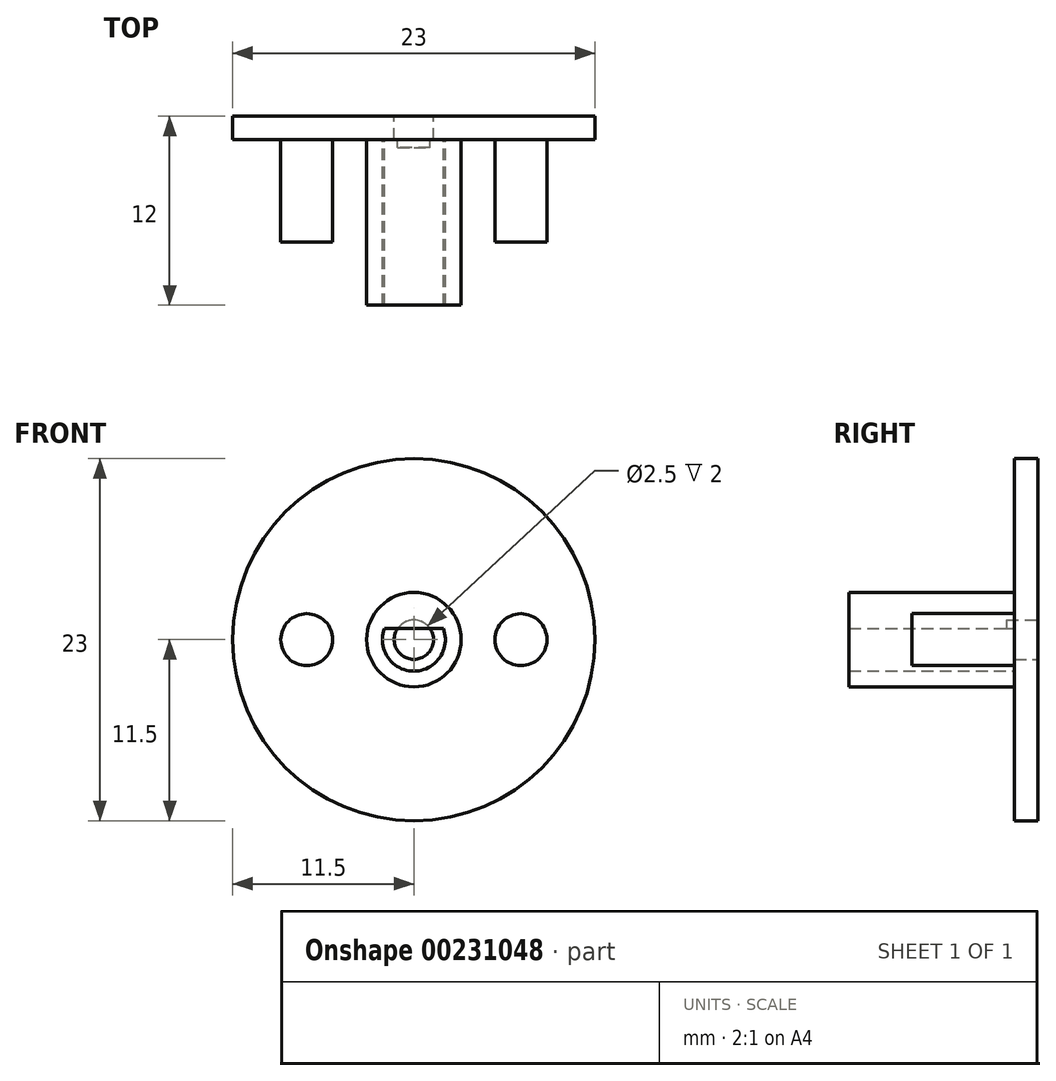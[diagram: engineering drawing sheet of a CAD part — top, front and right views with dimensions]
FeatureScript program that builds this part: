
annotation { "Feature Type Name" : "Feature", "Feature Type Description" : "" }
export const myFeature = defineFeature(function(context is Context, id is Id, definition is map)
    precondition{}
    {
        {
            var Q0;
            Q0=qCreatedBy(makeId("Front.planeOp"),FACE);
            var sketch = newSketch(context, id + "F0", { "sketchPlane" : qUnion([Q0])});
            skCircle(sketch, "E0", {"center": v(0, 0) * mm, "radius": 3 * mm});
            skCircle(sketch, "E1", {"center": v(6.5, 0) * mm, "radius": 1.8 * mm});
            skCircle(sketch, "E2", {"center": v(0, 0) * mm, "radius": 11.5 * mm});
            skSolve(sketch);
        }
        {
            var Q0;
            Q0=makeQuery(id+"F0.imprint","IMPRINT",FACE,{"disambiguationData":[TD([[makeQuery(id+"F0.imprint","IMPRINT",EDGE,{"derivedFrom":sQuery(id+"F0.wireOp",EDGE,"E0")}),-1.0]])]});
            var Q1;
            Q1=makeQuery(id+"F0.imprint","IMPRINT",FACE,{"disambiguationData":[TD([[makeQuery(id+"F0.imprint","IMPRINT",EDGE,{"derivedFrom":sQuery(id+"F0.wireOp",EDGE,"E0")}),1.0]])]});
            var Q2;
            Q2=makeQuery(id+"F0.imprint","IMPRINT",FACE,{"disambiguationData":[TD([[makeQuery(id+"F0.imprint","IMPRINT",EDGE,{"derivedFrom":sQuery(id+"F0.wireOp",EDGE,"E1")}),1.0]])]});
            extrude(context, id + "F1", {"entities" : qUnion([Q0, Q1, Q2]), "depth" : 1.5 * mm});
        }
        {
            var Q0;
            Q0=makeQuery(id+"F1.opExtrude","CAP_FACE",FACE,{"disambiguationData":[OSD([sQuery(id+"F0.wireOp",EDGE,"E2")])],"isStart":false});
            var sketch = newSketch(context, id + "F2", { "sketchPlane" : qUnion([Q0])});
            skCircle(sketch, "E3", {"center": v(0, 0) * mm, "radius": 3 * mm});
            skCircle(sketch, "E4", {"center": v(6.8, 0) * mm, "radius": 1.65 * mm});
            skCircle(sketch, "E5", {"center": v(-6.8, 0) * mm, "radius": 1.65 * mm});
            skCircle(sketch, "E6", {"center": v(0, 0) * mm, "radius": 2 * mm});
            skLineSegment(sketch, "E7", {"start": v(-1.87, 0.7) * mm, "end": v(1.87, 0.7) * mm});
            skSolve(sketch);
        }
        {
            var Q0;
            Q0=makeQuery(id+"F2.imprint","IMPRINT",FACE,{"disambiguationData":[TD([[makeQuery(id+"F2.imprint","IMPRINT",EDGE,{"derivedFrom":sQuery(id+"F2.wireOp",EDGE,"E5")}),1.0]])]});
            var Q1;
            Q1=makeQuery(id+"F2.imprint","IMPRINT",FACE,{"disambiguationData":[TD([[makeQuery(id+"F2.imprint","IMPRINT",EDGE,{"derivedFrom":sQuery(id+"F2.wireOp",EDGE,"E3")}),1.0]])]});
            var Q2;
            {var subQ0=sQuery(id+"F2.wireOp",EDGE,"E7");Q2=makeQuery(id+"F2.imprint","IMPRINT",FACE,{"disambiguationData":[TD([[makeQuery(id+"F2.imprint","IMPRINT",EDGE,{"derivedFrom":subQ0}),1.0]])]});}
            var Q3;
            Q3=makeQuery(id+"F2.imprint","IMPRINT",FACE,{"disambiguationData":[TD([[makeQuery(id+"F2.imprint","IMPRINT",EDGE,{"derivedFrom":sQuery(id+"F2.wireOp",EDGE,"E4")}),1.0]])]});
            extrude(context, id + "F3", {"entities" : qUnion([Q0, Q1, Q2, Q3]), "operationType" : NewBodyOperationType.ADD, "depth" : 6.5 * mm});
        }
        {
            var Q0;
            Q0=makeQuery(id+"F3.opExtrude","CAP_FACE",FACE,{"disambiguationData":[OSD([sQuery(id+"F2.wireOp",EDGE,"E3"),sQuery(id+"F2.wireOp",EDGE,"E6"),sQuery(id+"F2.wireOp",EDGE,"E7")])],"isStart":false});
            extrude(context, id + "F4", {"entities" : qUnion([Q0]), "operationType" : NewBodyOperationType.ADD, "depth" : 4 * mm});
        }
        {
            var Q0;
            Q0=makeQuery(id+"F1.opExtrude","CAP_FACE",FACE,{"disambiguationData":[OSD([sQuery(id+"F0.wireOp",EDGE,"E2")])],"isStart":true});
            var sketch = newSketch(context, id + "F5", { "sketchPlane" : qUnion([Q0])});
            skCircle(sketch, "E8", {"center": v(0, 0) * mm, "radius": 1.25 * mm});
            skSolve(sketch);
        }
        {
            var Q0;
            Q0=makeQuery(id+"F5.imprint","IMPRINT",FACE,{"disambiguationData":[TD([[makeQuery(id+"F5.imprint","IMPRINT",EDGE,{"derivedFrom":sQuery(id+"F5.wireOp",EDGE,"E8")}),1.0]])]});
            extrude(context, id + "F6", {"entities" : qUnion([Q0]), "operationType" : NewBodyOperationType.REMOVE, "oppositeDirection" : true, "depth" : 2 * mm});
        }
    });
